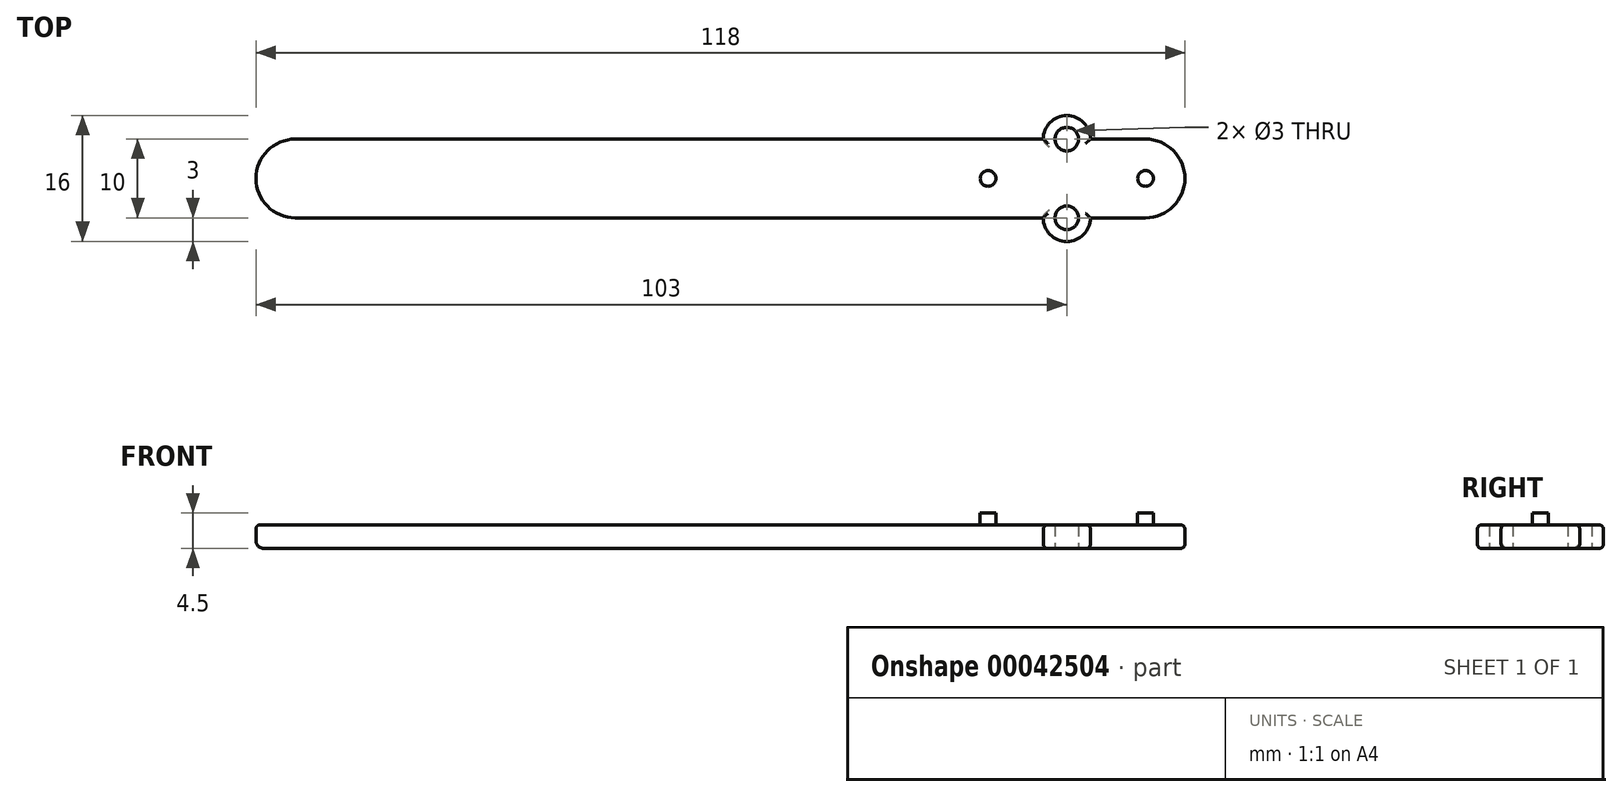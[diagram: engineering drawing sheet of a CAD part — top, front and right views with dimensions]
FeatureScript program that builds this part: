
annotation { "Feature Type Name" : "Feature", "Feature Type Description" : "" }
export const myFeature = defineFeature(function(context is Context, id is Id, definition is map)
    precondition{}
    {
        {
            var Q0;
            Q0=qCreatedBy(makeId("Top.planeOp"),FACE);
            var sketch = newSketch(context, id + "F0", { "sketchPlane" : qUnion([Q0])});
            skLineSegment(sketch, "E0.bottom", {"start": v(0, 0) * mm, "end": v(-95, 0) * mm});
            skLineSegment(sketch, "E0.top", {"start": v(0, 10) * mm, "end": v(-95, 10) * mm});
            skLineSegment(sketch, "E0.right", {"start": v(-100, 5) * mm, "end": v(-100, 5) * mm});
            skPoint(sketch, "E1.visualSharp", {"position": v(-100, 10) * mm});
            skArc(sketch, "E1.filletArc", {"start": v(-95, 10) * mm, "mid": v(-98.54, 8.54) * mm, "end": v(-100, 5) * mm});
            skPoint(sketch, "E2.visualSharp", {"position": v(-100, 0) * mm});
            skArc(sketch, "E2.filletArc", {"start": v(-100, 5) * mm, "mid": v(-98.54, 1.46) * mm, "end": v(-95, 0) * mm});
            skArc(sketch, "E3", {"start": v(6, 10) * mm, "mid": v(3, 13) * mm, "end": v(0, 10) * mm});
            skArc(sketch, "E4", {"start": v(0, 0) * mm, "mid": v(3, -3) * mm, "end": v(6, 0) * mm});
            skCircle(sketch, "E5", {"center": v(3, 10) * mm, "radius": 1.5 * mm});
            skCircle(sketch, "E6", {"center": v(3, 0) * mm, "radius": 1.5 * mm});
            skLineSegment(sketch, "E7.bottom", {"start": v(6, 10) * mm, "end": v(13, 10) * mm});
            skLineSegment(sketch, "E7.top", {"start": v(6, 0) * mm, "end": v(13, 0) * mm});
            skLineSegment(sketch, "E7.left", {"start": v(6, 10) * mm, "end": v(6, 0) * mm, "construction": true});
            skLineSegment(sketch, "E7.right", {"start": v(18, 5) * mm, "end": v(18, 5) * mm});
            skPoint(sketch, "E8.visualSharp", {"position": v(18, 10) * mm});
            skArc(sketch, "E8.filletArc", {"start": v(18, 5) * mm, "mid": v(16.54, 8.54) * mm, "end": v(13, 10) * mm});
            skPoint(sketch, "E9.visualSharp", {"position": v(18, 0) * mm});
            skArc(sketch, "E9.filletArc", {"start": v(13, 0) * mm, "mid": v(16.54, 1.46) * mm, "end": v(18, 5) * mm});
            skLineSegment(sketch, "E10", {"start": v(13, 5) * mm, "end": v(0, 5) * mm, "construction": true});
            skLineSegment(sketch, "E11", {"start": v(3, 10) * mm, "end": v(3, 0) * mm, "construction": true});
            skPoint(sketch, "E12", {"position": v(-7, 5) * mm});
            skSolve(sketch);
        }
        {
            var Q0;
            Q0 = qSketchRegion(id + "F0", true);
            var Q1;
            Q1=makeQuery(id+"F0.imprint","IMPRINT",FACE,{"disambiguationData":[TD([[makeQuery(id+"F0.imprint","IMPRINT",EDGE,{"derivedFrom":sQuery(id+"F0.wireOp",EDGE,"E0.bottom")}),-1.0]])]});
            extrude(context, id + "F1", {"entities" : qUnion([Q0, Q1]), "depth" : 3 * mm});
        }
        {
            var Q0;
            Q0=makeQuery(id+"F1.opExtrude","CAP_EDGE",EDGE,{"disambiguationData":[OSD([sQuery(id+"F0.wireOp",EDGE,"E0.bottom")])],"isStart":false});
            fillet(context, id + "F2", {"entities" : qUnion([Q0]), "radius" : 0.55 * mm, "tangentPropagation" : true, "allowEdgeOverflow" : false});
        }
        {
            var Q0;
            Q0=makeQuery(id+"F1.opExtrude","CAP_EDGE",EDGE,{"disambiguationData":[OSD([sQuery(id+"F0.wireOp",EDGE,"E0.bottom")])],"isStart":true});
            fillet(context, id + "F3", {"entities" : qUnion([Q0]), "radius" : 1 * mm, "tangentPropagation" : true, "allowEdgeOverflow" : false});
        }
        {
            var Q0;
            Q0=makeQuery(id+"F1.opExtrude","CAP_EDGE",EDGE,{"disambiguationData":[OSD([sQuery(id+"F0.wireOp",EDGE,"E4")])],"isStart":false});
            var Q1;
            Q1=makeQuery(id+"F1.opExtrude","CAP_EDGE",EDGE,{"disambiguationData":[OSD([sQuery(id+"F0.wireOp",EDGE,"75a8fdf6-88b0-4338-b9ba-6ad033f037c1")])],"isStart":false});
            var Q2;
            Q2=makeQuery(id+"F1.opExtrude","CAP_EDGE",EDGE,{"disambiguationData":[OSD([sQuery(id+"F0.wireOp",EDGE,"E3")])],"isStart":false});
            var Q3;
            Q3=makeQuery(id+"F1.opExtrude","CAP_EDGE",EDGE,{"disambiguationData":[OSD([sQuery(id+"F0.wireOp",EDGE,"E4")])],"isStart":true});
            var Q4;
            Q4=makeQuery(id+"F1.opExtrude","CAP_EDGE",EDGE,{"disambiguationData":[OSD([sQuery(id+"F0.wireOp",EDGE,"75a8fdf6-88b0-4338-b9ba-6ad033f037c1")])],"isStart":true});
            var Q5;
            Q5=makeQuery(id+"F1.opExtrude","CAP_EDGE",EDGE,{"disambiguationData":[OSD([sQuery(id+"F0.wireOp",EDGE,"E3")])],"isStart":true});
            var Q6;
            Q6=makeQuery(id+"F1.opExtrude","CAP_EDGE",EDGE,{"disambiguationData":[OSD([sQuery(id+"F0.wireOp",EDGE,"E7.top")])],"isStart":false});
            var Q7;
            Q7=makeQuery(id+"F1.opExtrude","CAP_EDGE",EDGE,{"disambiguationData":[OSD([sQuery(id+"F0.wireOp",EDGE,"E8.filletArc"),sQuery(id+"F0.wireOp",EDGE,"E9.filletArc")])],"isStart":false});
            var Q8;
            Q8=makeQuery(id+"F1.opExtrude","CAP_EDGE",EDGE,{"disambiguationData":[OSD([sQuery(id+"F0.wireOp",EDGE,"E8.filletArc"),sQuery(id+"F0.wireOp",EDGE,"E9.filletArc")])],"isStart":true});
            var Q9;
            Q9=makeQuery(id+"F1.opExtrude","CAP_EDGE",EDGE,{"disambiguationData":[OSD([sQuery(id+"F0.wireOp",EDGE,"E7.top")])],"isStart":true});
            var Q10;
            Q10=makeQuery(id+"F1.opExtrude","CAP_EDGE",EDGE,{"disambiguationData":[OSD([sQuery(id+"F0.wireOp",EDGE,"E7.bottom")])],"isStart":true});
            var Q11;
            Q11=makeQuery(id+"F1.opExtrude","CAP_EDGE",EDGE,{"disambiguationData":[OSD([sQuery(id+"F0.wireOp",EDGE,"E7.bottom")])],"isStart":false});
            fillet(context, id + "F4", {"entities" : qUnion([Q0, Q1, Q2, Q3, Q4, Q5, Q6, Q7, Q8, Q9, Q10, Q11]), "radius" : 0.55 * mm, "tangentPropagation" : true, "allowEdgeOverflow" : false});
        }
        {
            var Q0;
            Q0=qCreatedBy(makeId("Top.planeOp"),FACE);
            var sketch = newSketch(context, id + "F5", { "sketchPlane" : qUnion([Q0])});
            skCircle(sketch, "E13", {"center": v(13, 5) * mm, "radius": 1 * mm});
            skCircle(sketch, "E14", {"center": v(-7, 5) * mm, "radius": 1 * mm});
            skSolve(sketch);
        }
        {
            var Q0;
            Q0 = qSketchRegion(id + "F5", true);
            extrude(context, id + "F6", {"entities" : qUnion([Q0]), "operationType" : NewBodyOperationType.ADD, "depth" : 4.5 * mm});
        }
    });
